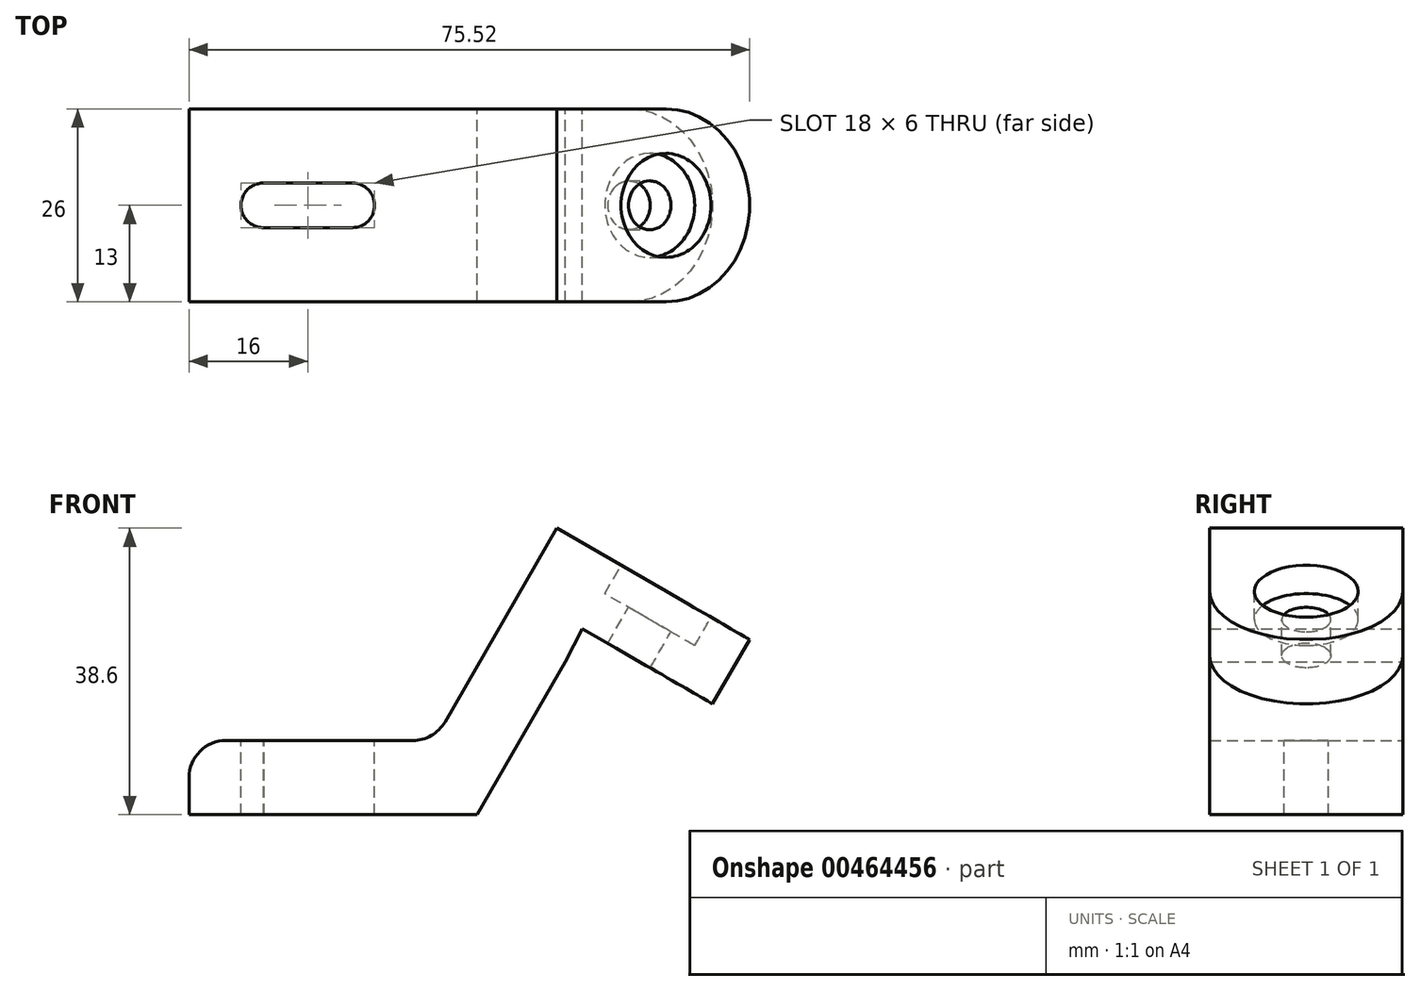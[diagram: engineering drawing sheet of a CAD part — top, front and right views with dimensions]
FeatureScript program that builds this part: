
annotation { "Feature Type Name" : "Feature", "Feature Type Description" : "" }
export const myFeature = defineFeature(function(context is Context, id is Id, definition is map)
    precondition{}
    {
        {
            var Q0;
            Q0=qCreatedBy(makeId("Front.planeOp"),FACE);
            var sketch = newSketch(context, id + "F0", { "sketchPlane" : qUnion([Q0])});
            skLineSegment(sketch, "E0", {"start": v(0, 0) * mm, "end": v(-38.8, 0) * mm});
            skLineSegment(sketch, "E1", {"start": v(0, 0) * mm, "end": v(11.9, 20.61) * mm});
            skLineSegment(sketch, "E2", {"start": v(-38.8, 0) * mm, "end": v(-38.8, 5) * mm});
            skLineSegment(sketch, "E3", {"start": v(-33.8, 10) * mm, "end": v(-8.66, 10) * mm});
            skLineSegment(sketch, "E4", {"start": v(19.4, 33.6) * mm, "end": v(10.74, 38.6) * mm});
            skLineSegment(sketch, "E5", {"start": v(-4.33, 12.5) * mm, "end": v(10.74, 38.6) * mm});
            skLineSegment(sketch, "E6", {"start": v(19.4, 33.6) * mm, "end": v(36.72, 23.6) * mm});
            skLineSegment(sketch, "E7", {"start": v(36.72, 23.6) * mm, "end": v(31.72, 14.94) * mm});
            skLineSegment(sketch, "E8", {"start": v(31.72, 14.94) * mm, "end": v(18.73, 22.44) * mm});
            skPoint(sketch, "E9", {"position": v(-38.8, 10) * mm});
            skArc(sketch, "E10.filletArc", {"start": v(-33.8, 10) * mm, "mid": v(-37.34, 8.54) * mm, "end": v(-38.8, 5) * mm});
            skPoint(sketch, "E11", {"position": v(-5.77, 10) * mm});
            skArc(sketch, "E12.filletArc", {"start": v(-8.66, 10) * mm, "mid": v(-6.16, 10.67) * mm, "end": v(-4.33, 12.5) * mm});
            skPoint(sketch, "E13.newPointB", {"position": v(19.4, 33.6) * mm});
            skLineSegment(sketch, "E14", {"start": v(11.9, 20.61) * mm, "end": v(14.16, 25.07) * mm});
            skLineSegment(sketch, "E15", {"start": v(14.16, 25.07) * mm, "end": v(18.73, 22.44) * mm});
            skSolve(sketch);
        }
        {
            var Q0;
            {var subQ0=sQuery(id+"F0.wireOp",EDGE,"E6");Q0=makeQuery(id+"F0.imprint","IMPRINT",FACE,{"disambiguationData":[TD([[makeQuery(id+"F0.imprint","IMPRINT",EDGE,{"derivedFrom":subQ0}),-1.0]])]});}
            var Q1;
            {var subQ3=sQuery(id+"F0.wireOp",EDGE,"E0");Q1=makeQuery(id+"F0.imprint","IMPRINT",FACE,{"disambiguationData":[TD([[makeQuery(id+"F0.imprint","IMPRINT",EDGE,{"derivedFrom":subQ3}),-1.0]])]});}
            extrude(context, id + "F1", {"entities" : qUnion([Q0, Q1]), "depth" : 26 * mm, "offsetDistance" : 25 * mm});
        }
        {
            var Q0;
            Q0=makeQuery(id+"F1.opExtrude","SWEPT_FACE",FACE,{"disambiguationData":[OSD([sQuery(id+"F0.wireOp",EDGE,"E3")])]});
            var sketch = newSketch(context, id + "F2", { "sketchPlane" : qUnion([Q0])});
            skCircle(sketch, "E16", {"center": v(-28.8, -13) * mm, "radius": 3 * mm});
            skPoint(sketch, "E16.centerSnap0", {"position": v(-33.8, -13) * mm});
            skCircle(sketch, "E17", {"center": v(-16.8, -13) * mm, "radius": 3 * mm});
            skLineSegment(sketch, "E18", {"start": v(-28.72, -10) * mm, "end": v(-16.8, -10) * mm});
            skLineSegment(sketch, "E19", {"start": v(-28.84, -16) * mm, "end": v(-16.8, -16) * mm});
            skSolve(sketch);
        }
        {
            var Q0;
            Q0 = qSketchRegion(id + "F2", true);
            extrude(context, id + "F3", {"entities" : qUnion([Q0]), "operationType" : NewBodyOperationType.REMOVE, "endBound" : BoundingType.THROUGH_ALL, "oppositeDirection" : true, "depth" : 25 * mm, "offsetDistance" : 25 * mm});
        }
        {
            var Q0;
            Q0=makeQuery(id+"F1.opExtrude","CAP_EDGE",EDGE,{"disambiguationData":[OSD([sQuery(id+"F0.wireOp",EDGE,"E7")])],"isStart":false});
            var Q1;
            Q1=makeQuery(id+"F1.opExtrude","CAP_EDGE",EDGE,{"disambiguationData":[OSD([sQuery(id+"F0.wireOp",EDGE,"E7")])],"isStart":true});
            fillet(context, id + "F4", {"entities" : qUnion([Q0, Q1]), "radius" : 13 * mm, "tangentPropagation" : true, "allowEdgeOverflow" : false});
        }
        {
            var Q0;
            Q0=makeQuery(id+"F1.opExtrude","SWEPT_FACE",FACE,{"disambiguationData":[OSD([sQuery(id+"F0.wireOp",EDGE,"E4"),sQuery(id+"F0.wireOp",EDGE,"E6")])]});
            var sketch = newSketch(context, id + "F5", { "sketchPlane" : qUnion([Q0])});
            skCircle(sketch, "E20", {"center": v(7, -13) * mm, "radius": 7 * mm});
            skSolve(sketch);
        }
        {
            var Q0;
            Q0 = qSketchRegion(id + "F5", true);
            extrude(context, id + "F6", {"entities" : qUnion([Q0]), "operationType" : NewBodyOperationType.REMOVE, "oppositeDirection" : true, "depth" : 4.4 * mm, "offsetDistance" : 25 * mm});
        }
        {
            var Q0;
            Q0=makeQuery(id+"F6.boolean.opBoolean","COPY",FACE,{"derivedFrom":makeQuery(id+"F6.opExtrude","CAP_FACE",FACE,{"disambiguationData":[OSD([sQuery(id+"F5.wireOp",EDGE,"E20")])],"isStart":false})});
            var sketch = newSketch(context, id + "F7", { "sketchPlane" : qUnion([Q0])});
            skCircle(sketch, "E21", {"center": v(7, -13) * mm, "radius": 3.3 * mm});
            skSolve(sketch);
        }
        {
            var Q0;
            Q0 = qSketchRegion(id + "F7", true);
            extrude(context, id + "F8", {"entities" : qUnion([Q0]), "operationType" : NewBodyOperationType.REMOVE, "endBound" : BoundingType.THROUGH_ALL, "oppositeDirection" : true, "depth" : 25 * mm, "offsetDistance" : 25 * mm});
        }
    });
